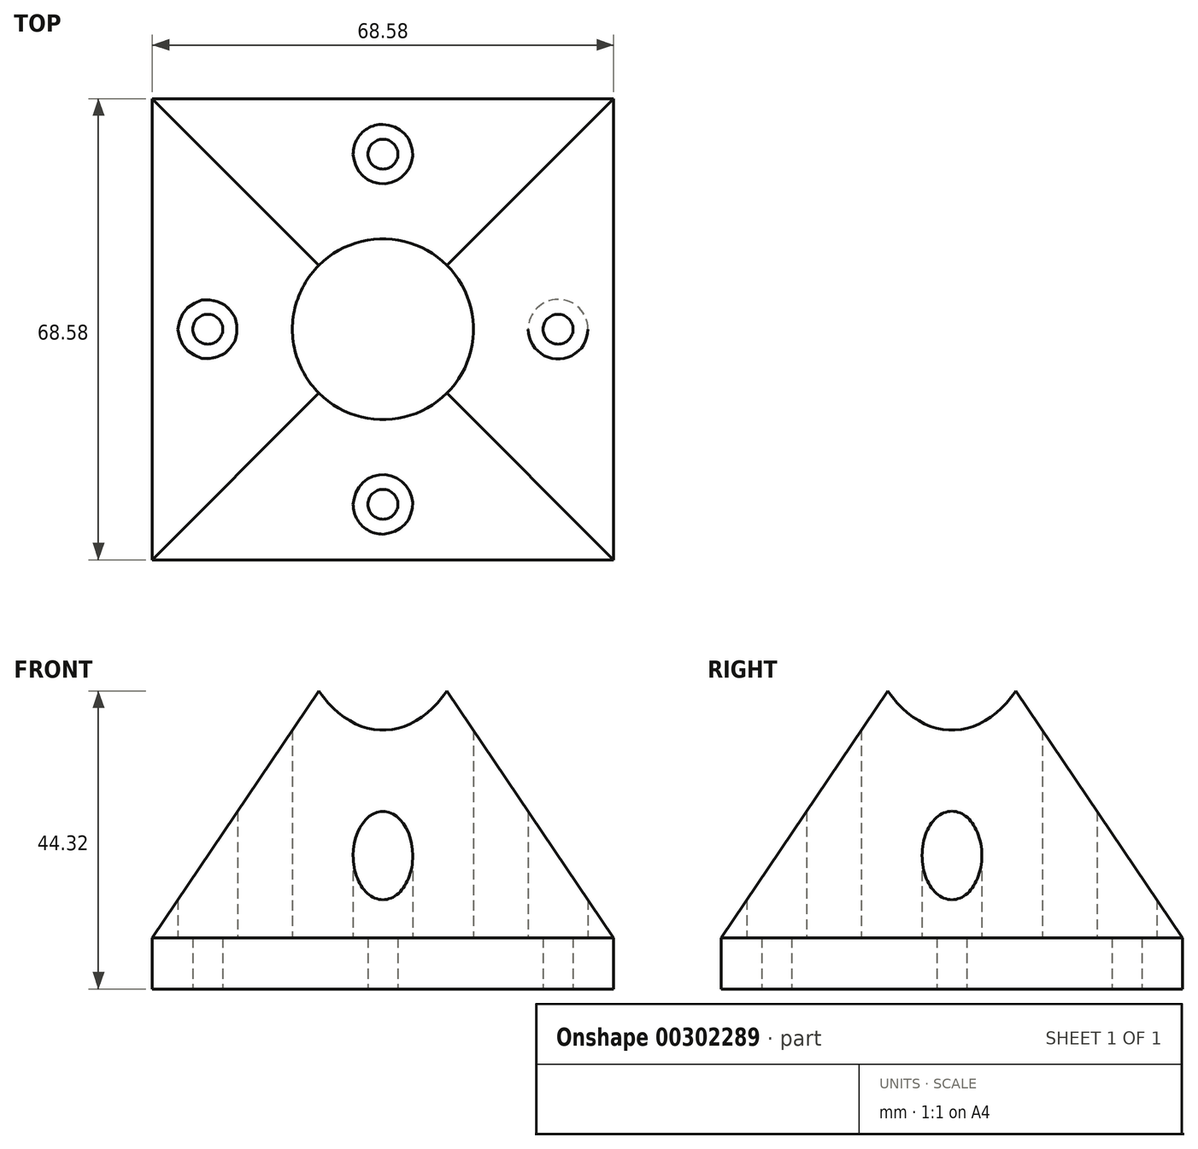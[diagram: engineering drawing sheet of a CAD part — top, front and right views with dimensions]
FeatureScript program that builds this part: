
annotation { "Feature Type Name" : "Feature", "Feature Type Description" : "" }
export const myFeature = defineFeature(function(context is Context, id is Id, definition is map)
    precondition{}
    {
        {
            var Q0;
            Q0=qCreatedBy(makeId("Front.planeOp"),FACE);
            var sketch = newSketch(context, id + "F0", { "sketchPlane" : qUnion([Q0])});
            skLineSegment(sketch, "E0", {"start": v(-34.3, 0) * mm, "end": v(0, 50.8) * mm});
            skLineSegment(sketch, "E1", {"start": v(34.3, 0) * mm, "end": v(0, 50.8) * mm});
            skLineSegment(sketch, "E2", {"start": v(-34.3, 0) * mm, "end": v(34.3, 0) * mm});
            skLineSegment(sketch, "E3", {"start": v(34.3, -9.13) * mm, "end": v(0, -9.13) * mm, "construction": true});
            skLineSegment(sketch, "E4", {"start": v(0, -9.13) * mm, "end": v(-34.3, -9.13) * mm, "construction": true});
            skSolve(sketch);
        }
        {
            var Q0;
            Q0 = qSketchRegion(id + "F0", true);
            var Q1;
            Q1=sQuery(id+"F0.wireOp",EDGE,"E0");
            var Q2;
            Q2=sQuery(id+"F0.wireOp",EDGE,"E1");
            var Q3;
            Q3=sQuery(id+"F0.wireOp",EDGE,"E2");
            extrude(context, id + "F1", {"entities" : qUnion([Q0]), "surfaceEntities" : qUnion([Q1, Q2, Q3]), "endBound" : BoundingType.SYMMETRIC, "depth" : 68.58 * mm});
        }
        {
            var Q0;
            Q0=qCreatedBy(makeId("Right.planeOp"),FACE);
            var sketch = newSketch(context, id + "F2", { "sketchPlane" : qUnion([Q0])});
            skLineSegment(sketch, "E5", {"start": v(34.3, 0) * mm, "end": v(0, 50.8) * mm});
            skLineSegment(sketch, "E6", {"start": v(0, 50.8) * mm, "end": v(-34.3, 0) * mm});
            skLineSegment(sketch, "E7", {"start": v(34.3, 0) * mm, "end": v(-34.3, 0) * mm});
            skLineSegment(sketch, "E8", {"start": v(34.3, -5.3) * mm, "end": v(0, -5.3) * mm});
            skLineSegment(sketch, "E9", {"start": v(0, -5.3) * mm, "end": v(-34.3, -5.3) * mm});
            skSolve(sketch);
        }
        {
            var Q0;
            Q0 = qSketchRegion(id + "F2", true);
            var Q1;
            Q1=sQuery(id+"F2.wireOp",EDGE,"E6");
            var Q2;
            Q2=sQuery(id+"F2.wireOp",EDGE,"E5");
            var Q3;
            Q3=sQuery(id+"F2.wireOp",EDGE,"E7");
            extrude(context, id + "F3", {"entities" : qUnion([Q0]), "surfaceEntities" : qUnion([Q1, Q2, Q3]), "endBound" : BoundingType.SYMMETRIC, "depth" : 68.58 * mm});
        }
        {
            var Q0;
            Q0=qCreatedBy(makeId("Front.planeOp"),FACE);
            var sketch = newSketch(context, id + "F4", { "sketchPlane" : qUnion([Q0])});
            skLineSegment(sketch, "E10", {"start": v(0, 50.8) * mm, "end": v(-34.3, 0) * mm});
            skLineSegment(sketch, "E11", {"start": v(-34.3, 0) * mm, "end": v(-34.3, 50.8) * mm});
            skLineSegment(sketch, "E12", {"start": v(-34.3, 50.8) * mm, "end": v(0, 50.8) * mm});
            skLineSegment(sketch, "E13", {"start": v(34.3, 50.8) * mm, "end": v(34.3, 0) * mm});
            skLineSegment(sketch, "E14", {"start": v(34.3, 0) * mm, "end": v(0, 50.8) * mm});
            skSolve(sketch);
        }
        {
            var Q0;
            Q0 = qSketchRegion(id + "F4", true);
            extrude(context, id + "F5", {"entities" : qUnion([Q0]), "operationType" : NewBodyOperationType.REMOVE, "endBound" : BoundingType.SYMMETRIC, "depth" : 76.2 * mm});
        }
        {
            var Q0;
            Q0=qCreatedBy(makeId("Front.planeOp"),FACE);
            var sketch = newSketch(context, id + "F6", { "sketchPlane" : qUnion([Q0])});
            skLineSegment(sketch, "E15", {"start": v(0, 50.8) * mm, "end": v(34.3, 0) * mm});
            skLineSegment(sketch, "E16", {"start": v(34.3, 0) * mm, "end": v(34.3, 50.8) * mm});
            skLineSegment(sketch, "E17", {"start": v(34.3, 50.8) * mm, "end": v(0, 50.8) * mm});
            skSolve(sketch);
        }
        {
            var Q0;
            Q0 = qSketchRegion(id + "F6", true);
            extrude(context, id + "F7", {"entities" : qUnion([Q0]), "operationType" : NewBodyOperationType.REMOVE, "endBound" : BoundingType.SYMMETRIC, "oppositeDirection" : true, "depth" : 76.2 * mm});
        }
        {
            var Q0;
            Q0=qCreatedBy(makeId("Right.planeOp"),FACE);
            var sketch = newSketch(context, id + "F8", { "sketchPlane" : qUnion([Q0])});
            skLineSegment(sketch, "E18", {"start": v(57.27, 50.8) * mm, "end": v(57.27, 0) * mm, "construction": true});
            skLineSegment(sketch, "E19", {"start": v(34.3, 57.76) * mm, "end": v(0, 57.76) * mm, "construction": true});
            skLineSegment(sketch, "E20", {"start": v(0, 57.76) * mm, "end": v(-34.3, 57.76) * mm, "construction": true});
            skLineSegment(sketch, "E21", {"start": v(0, 50.8) * mm, "end": v(34.3, 0) * mm});
            skLineSegment(sketch, "E22", {"start": v(34.3, 0) * mm, "end": v(34.3, 50.8) * mm});
            skLineSegment(sketch, "E23", {"start": v(34.3, 50.8) * mm, "end": v(0, 50.8) * mm});
            skSolve(sketch);
        }
        {
            var Q0;
            Q0 = qSketchRegion(id + "F8", true);
            extrude(context, id + "F9", {"entities" : qUnion([Q0]), "operationType" : NewBodyOperationType.REMOVE, "endBound" : BoundingType.SYMMETRIC, "oppositeDirection" : true, "depth" : 76.2 * mm});
        }
        {
            var Q0;
            Q0=qCreatedBy(makeId("Right.planeOp"),FACE);
            var sketch = newSketch(context, id + "F10", { "sketchPlane" : qUnion([Q0])});
            skLineSegment(sketch, "E24", {"start": v(-53.98, 50.8) * mm, "end": v(-53.98, 0) * mm, "construction": true});
            skLineSegment(sketch, "E25", {"start": v(0, 56.14) * mm, "end": v(-34.3, 56.14) * mm, "construction": true});
            skLineSegment(sketch, "E26", {"start": v(0, 50.8) * mm, "end": v(-34.3, 50.8) * mm});
            skLineSegment(sketch, "E27", {"start": v(-34.3, 50.8) * mm, "end": v(-34.3, 0) * mm});
            skLineSegment(sketch, "E28", {"start": v(-34.3, 0) * mm, "end": v(0, 50.8) * mm});
            skSolve(sketch);
        }
        {
            var Q0;
            Q0 = qSketchRegion(id + "F10", true);
            extrude(context, id + "F11", {"entities" : qUnion([Q0]), "operationType" : NewBodyOperationType.REMOVE, "endBound" : BoundingType.SYMMETRIC, "oppositeDirection" : true, "depth" : 76.2 * mm});
        }
        {
            var Q0;
            Q0=makeQuery(id+"F3.opExtrude","SWEPT_FACE",FACE,{"disambiguationData":[OSD([sQuery(id+"F2.wireOp",EDGE,"E7")])]});
            var sketch = newSketch(context, id + "F12", { "sketchPlane" : qUnion([Q0])});
            skCircle(sketch, "E29", {"center": v(0, 0) * mm, "radius": 13.46 * mm});
            skSolve(sketch);
        }
        {
            var Q0;
            Q0 = qSketchRegion(id + "F12", true);
            extrude(context, id + "F13", {"entities" : qUnion([Q0]), "operationType" : NewBodyOperationType.REMOVE, "oppositeDirection" : true, "depth" : 53.34 * mm});
        }
        {
            var Q0;
            Q0=makeQuery(id+"F3.opExtrude","SWEPT_FACE",FACE,{"disambiguationData":[OSD([sQuery(id+"F2.wireOp",EDGE,"E7")])]});
            var sketch = newSketch(context, id + "F14", { "sketchPlane" : qUnion([Q0])});
            skCircle(sketch, "E30", {"center": v(0, 26.04) * mm, "radius": 4.45 * mm});
            skCircle(sketch, "E31", {"center": v(26.04, 0) * mm, "radius": 4.45 * mm});
            skCircle(sketch, "E32", {"center": v(0, -26.04) * mm, "radius": 4.45 * mm});
            skCircle(sketch, "E33", {"center": v(-26.04, 0) * mm, "radius": 4.45 * mm});
            skPoint(sketch, "E33.centerSnap0", {"position": v(-34.3, 0) * mm});
            skLineSegment(sketch, "E34", {"start": v(-34.3, 0) * mm, "end": v(-30.48, 0) * mm, "construction": true});
            skLineSegment(sketch, "E35", {"start": v(0, 34.3) * mm, "end": v(0, 30.48) * mm, "construction": true});
            skLineSegment(sketch, "E36", {"start": v(30.48, 0) * mm, "end": v(34.3, 0) * mm, "construction": true});
            skLineSegment(sketch, "E37", {"start": v(0, -30.48) * mm, "end": v(0, -34.3) * mm, "construction": true});
            skSolve(sketch);
        }
        {
            var Q0;
            Q0 = qSketchRegion(id + "F14", true);
            extrude(context, id + "F15", {"entities" : qUnion([Q0]), "operationType" : NewBodyOperationType.REMOVE, "oppositeDirection" : true, "depth" : 22.86 * mm});
        }
        {
            var Q0;
            Q0=makeQuery(id+"F1.opExtrude","SWEPT_FACE",FACE,{"disambiguationData":[OSD([sQuery(id+"F0.wireOp",EDGE,"E2")])]});
            var sketch = newSketch(context, id + "F16", { "sketchPlane" : qUnion([Q0])});
            skLineSegment(sketch, "E38.bottom", {"start": v(-34.29, 34.3) * mm, "end": v(34.3, 34.3) * mm});
            skLineSegment(sketch, "E38.top", {"start": v(-34.29, -34.3) * mm, "end": v(34.3, -34.3) * mm});
            skLineSegment(sketch, "E38.left", {"start": v(-34.29, 34.3) * mm, "end": v(-34.29, -34.3) * mm});
            skLineSegment(sketch, "E38.right", {"start": v(34.3, 34.3) * mm, "end": v(34.3, -34.3) * mm});
            skSolve(sketch);
        }
        {
            var Q0;
            Q0 = qSketchRegion(id + "F16", true);
            extrude(context, id + "F17", {"entities" : qUnion([Q0]), "depth" : 7.62 * mm});
        }
        {
            var Q0;
            Q0=makeQuery(id+"F17.opExtrude","CAP_FACE",FACE,{"disambiguationData":[OSD([sQuery(id+"F16.wireOp",EDGE,"E38.bottom"),sQuery(id+"F16.wireOp",EDGE,"E38.top"),sQuery(id+"F16.wireOp",EDGE,"E38.left"),sQuery(id+"F16.wireOp",EDGE,"E38.right")])],"isStart":false});
            var sketch = newSketch(context, id + "F18", { "sketchPlane" : qUnion([Q0])});
            skCircle(sketch, "E39", {"center": v(0, 26.04) * mm, "radius": 2.22 * mm});
            skCircle(sketch, "E40", {"center": v(-26.03, 0) * mm, "radius": 2.22 * mm});
            skCircle(sketch, "E41", {"center": v(0, -26.03) * mm, "radius": 2.22 * mm});
            skCircle(sketch, "E42", {"center": v(26.04, 0) * mm, "radius": 2.22 * mm});
            skLineSegment(sketch, "E43", {"start": v(-26.03, 0) * mm, "end": v(26.04, 0) * mm, "construction": true});
            skPoint(sketch, "E44", {"position": v(34.3, 0) * mm});
            skLineSegment(sketch, "E45", {"start": v(0, 26.04) * mm, "end": v(0, -26.03) * mm, "construction": true});
            skSolve(sketch);
        }
        {
            var Q0;
            Q0 = qSketchRegion(id + "F18", true);
            extrude(context, id + "F19", {"entities" : qUnion([Q0]), "operationType" : NewBodyOperationType.REMOVE, "oppositeDirection" : true, "depth" : 12.7 * mm});
        }
    });
